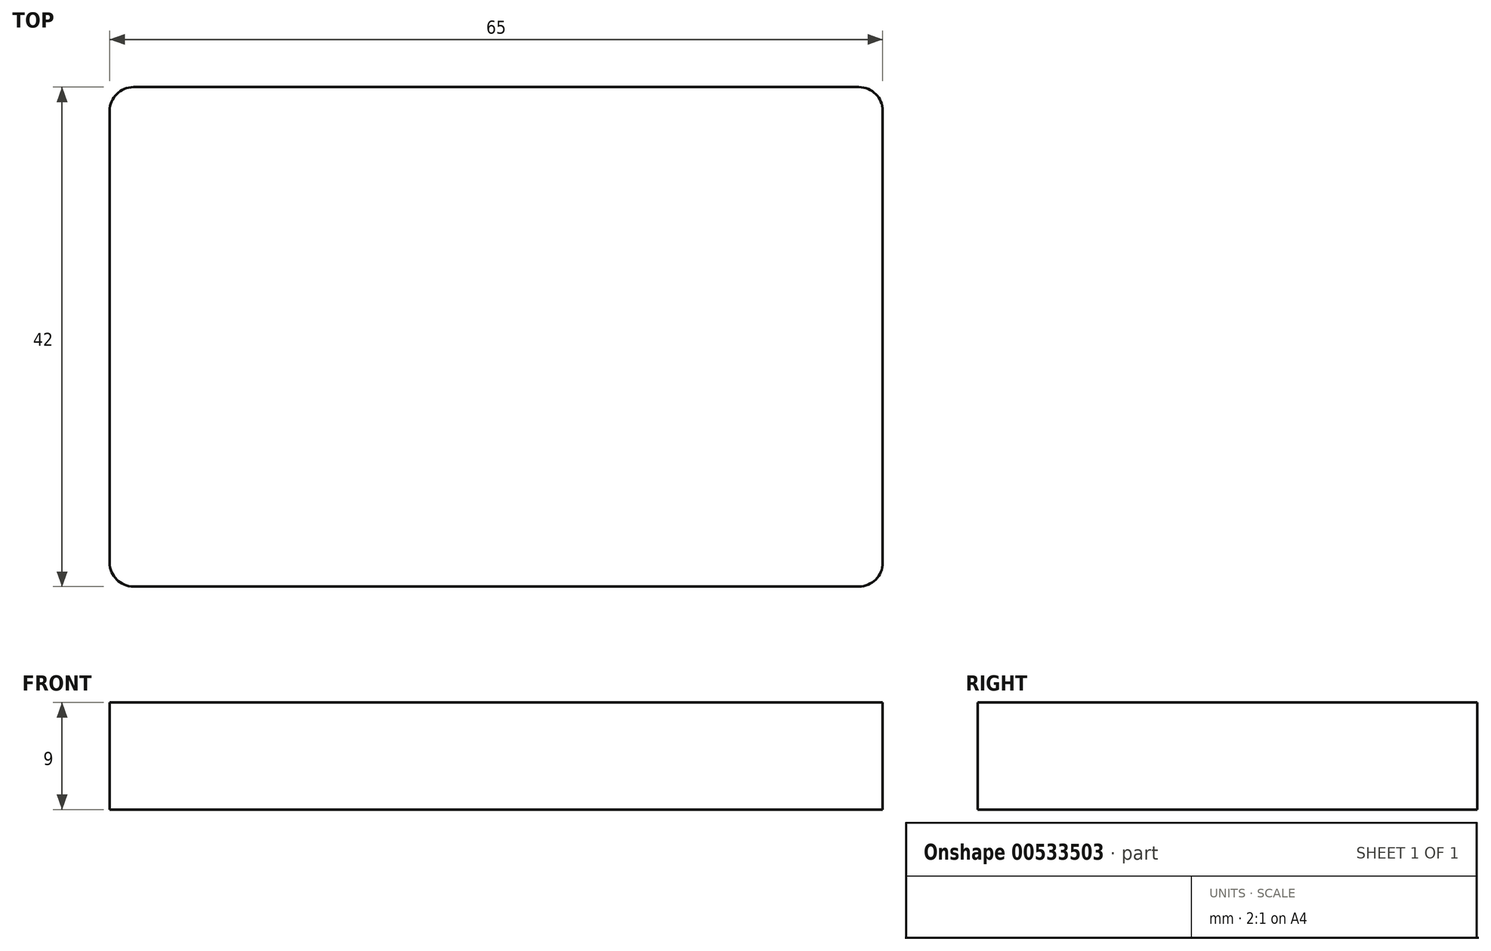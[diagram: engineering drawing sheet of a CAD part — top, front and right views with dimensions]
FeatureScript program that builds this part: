
annotation { "Feature Type Name" : "Feature", "Feature Type Description" : "" }
export const myFeature = defineFeature(function(context is Context, id is Id, definition is map)
    precondition{}
    {
        {
            var Q0;
            Q0=qCreatedBy(makeId("Top.planeOp"),FACE);
            var sketch = newSketch(context, id + "F0", { "sketchPlane" : qUnion([Q0])});
            skLineSegment(sketch, "E0.bottom", {"start": v(0, 0) * mm, "end": v(65, 0) * mm});
            skLineSegment(sketch, "E0.top", {"start": v(0, 42) * mm, "end": v(65, 42) * mm});
            skLineSegment(sketch, "E0.left", {"start": v(0, 0) * mm, "end": v(0, 42) * mm});
            skLineSegment(sketch, "E0.right", {"start": v(65, 0) * mm, "end": v(65, 42) * mm});
            skSolve(sketch);
        }
        {
            var Q0;
            Q0=qSketchRegion(id+"F0",true);
            extrude(context, id + "F1", {"entities" : qUnion([Q0]), "depth" : 9 * mm, "offsetDistance" : 25 * mm});
        }
        {
            var Q0;
            Q0=makeQuery(id+"F1.opExtrude","SWEPT_EDGE",EDGE,{"disambiguationData":[OSD([sQuery(id+"F0.wireOp",EDGE,"E0.bottom"),sQuery(id+"F0.wireOp",EDGE,"E0.left")])]});
            var Q1;
            Q1=makeQuery(id+"F1.opExtrude","SWEPT_EDGE",EDGE,{"disambiguationData":[OSD([sQuery(id+"F0.wireOp",EDGE,"E0.bottom"),sQuery(id+"F0.wireOp",EDGE,"E0.right")])]});
            var Q2;
            Q2=makeQuery(id+"F1.opExtrude","SWEPT_EDGE",EDGE,{"disambiguationData":[OSD([sQuery(id+"F0.wireOp",EDGE,"E0.top"),sQuery(id+"F0.wireOp",EDGE,"E0.right")])]});
            var Q3;
            Q3=makeQuery(id+"F1.opExtrude","SWEPT_EDGE",EDGE,{"disambiguationData":[OSD([sQuery(id+"F0.wireOp",EDGE,"E0.top"),sQuery(id+"F0.wireOp",EDGE,"E0.left")])]});
            fillet(context, id + "F2", {"entities" : qUnion([Q0, Q1, Q2, Q3]), "radius" : 2 * mm, "tangentPropagation" : true, "allowEdgeOverflow" : false});
        }
    });
